# Revit family: M_Plug Valve- 65-100 mm
name_source: partatom
category: Pipe Accessories
revit_build: Autodesk Revit MEP 2014 (Build: 20130308_1515(x64)
units: mm (PartAtom-declared; Revit-internal decimal feet)

## types (3) — shared parameters
Valve Material = PVC, Green

## per-type parameters (varying)
| type | Diameter 1 | Flange Diameter | Flange Radius | H2 | H3 | Height 1 | Height 2 | Height 3 | K Coefficient | Length 1 | Length 2 | Lever Length | Nominal Radius | Open Height | Outside Diameter | Outside Radius | Radius 1 | Radius 2 | Valve Length | Width 1 |
| 65 mm | 39 mm  [stored 0.127953 ft] | 175 mm  [stored 0.574147 ft] | 88 mm | 133 mm | 60 mm  [stored 0.19685 ft] | 89 mm | 72 mm | 36 mm | 0.44 | 100 mm  [stored 0.328084 ft] | 117 mm | 610 mm  [stored 2.00131 ft] | 33 mm | 145 mm  [stored 0.475722 ft] | 72 mm | 36 mm | 20 mm | 29 mm | 200 mm  [stored 0.656168 ft] | 49 mm |
| 80 mm | 48 mm  [stored 0.15748 ft] | 190 mm | 95 mm | 133 mm | 60 mm  [stored 0.19685 ft] | 95 mm | 88 mm | 44 mm | 1.07 | 100 mm  [stored 0.328084 ft] | 117 mm | 610 mm  [stored 2.00131 ft] | 40 mm | 145 mm  [stored 0.475722 ft] | 88 mm | 44 mm | 24 mm  [stored 0.0787402 ft] | 29 mm | 200 mm  [stored 0.656168 ft] | 60 mm  [stored 0.19685 ft] |
| 100 mm | 60 mm  [stored 0.19685 ft] | 225 mm  [stored 0.738189 ft] | 113 mm | 150 mm  [stored 0.492126 ft] | 68 mm | 114 mm | 110 mm  [stored 0.360892 ft] | 55 mm  [stored 0.180446 ft] | 1.07 | 113 mm | 132 mm  [stored 0.433071 ft] | 760 mm  [stored 2.49344 ft] | 50 mm | 180 mm  [stored 0.590551 ft] | 110 mm | 55 mm  [stored 0.180446 ft] | 30 mm  [stored 0.0984252 ft] | 33 mm  [stored 0.108268 ft] | 225 mm  [stored 0.738189 ft] | 75 mm  [stored 0.246063 ft] |

note: column(s) folded — value = type name in every type: Nominal Diameter

note: [stored X ft] marks values corroborated as IEEE doubles in the binary element streams (Revit-internal decimal feet)

## geometry (parser evidence)
native form markers: Blend x2, Sweep x1
no freeform markers — native parametric forms only
